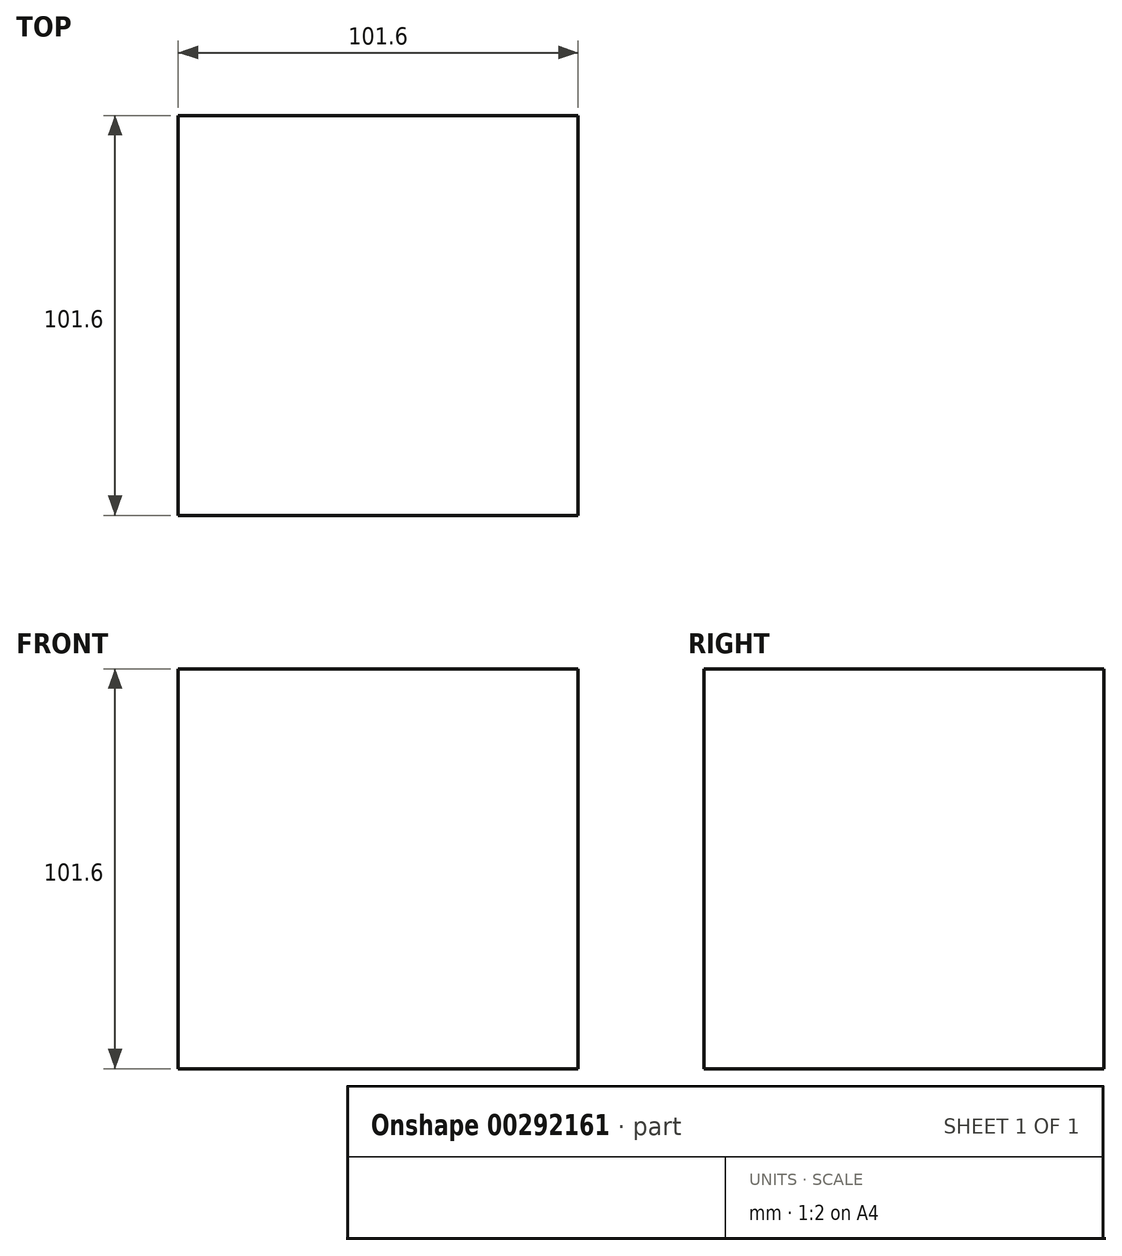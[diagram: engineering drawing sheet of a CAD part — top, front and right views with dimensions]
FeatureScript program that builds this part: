
annotation { "Feature Type Name" : "Feature", "Feature Type Description" : "" }
export const myFeature = defineFeature(function(context is Context, id is Id, definition is map)
    precondition{}
    {
        {
            var Q0;
            Q0=qCreatedBy(makeId("Front.planeOp"),FACE);
            var sketch = newSketch(context, id + "F0", { "sketchPlane" : qUnion([Q0])});
            skLineSegment(sketch, "E0.bottom", {"start": v(-50.56, -55.73) * mm, "end": v(51.04, -55.73) * mm});
            skLineSegment(sketch, "E0.top", {"start": v(-50.56, 45.87) * mm, "end": v(51.04, 45.87) * mm});
            skLineSegment(sketch, "E0.left", {"start": v(-50.56, -55.73) * mm, "end": v(-50.56, 45.87) * mm});
            skLineSegment(sketch, "E0.right", {"start": v(51.04, -55.73) * mm, "end": v(51.04, 45.87) * mm});
            skSolve(sketch);
        }
        {
            var Q0;
            Q0 = qSketchRegion(id + "F0", true);
            extrude(context, id + "F1", {"entities" : qUnion([Q0]), "endBound" : BoundingType.SYMMETRIC, "depth" : 101.6 * mm});
        }
    });
